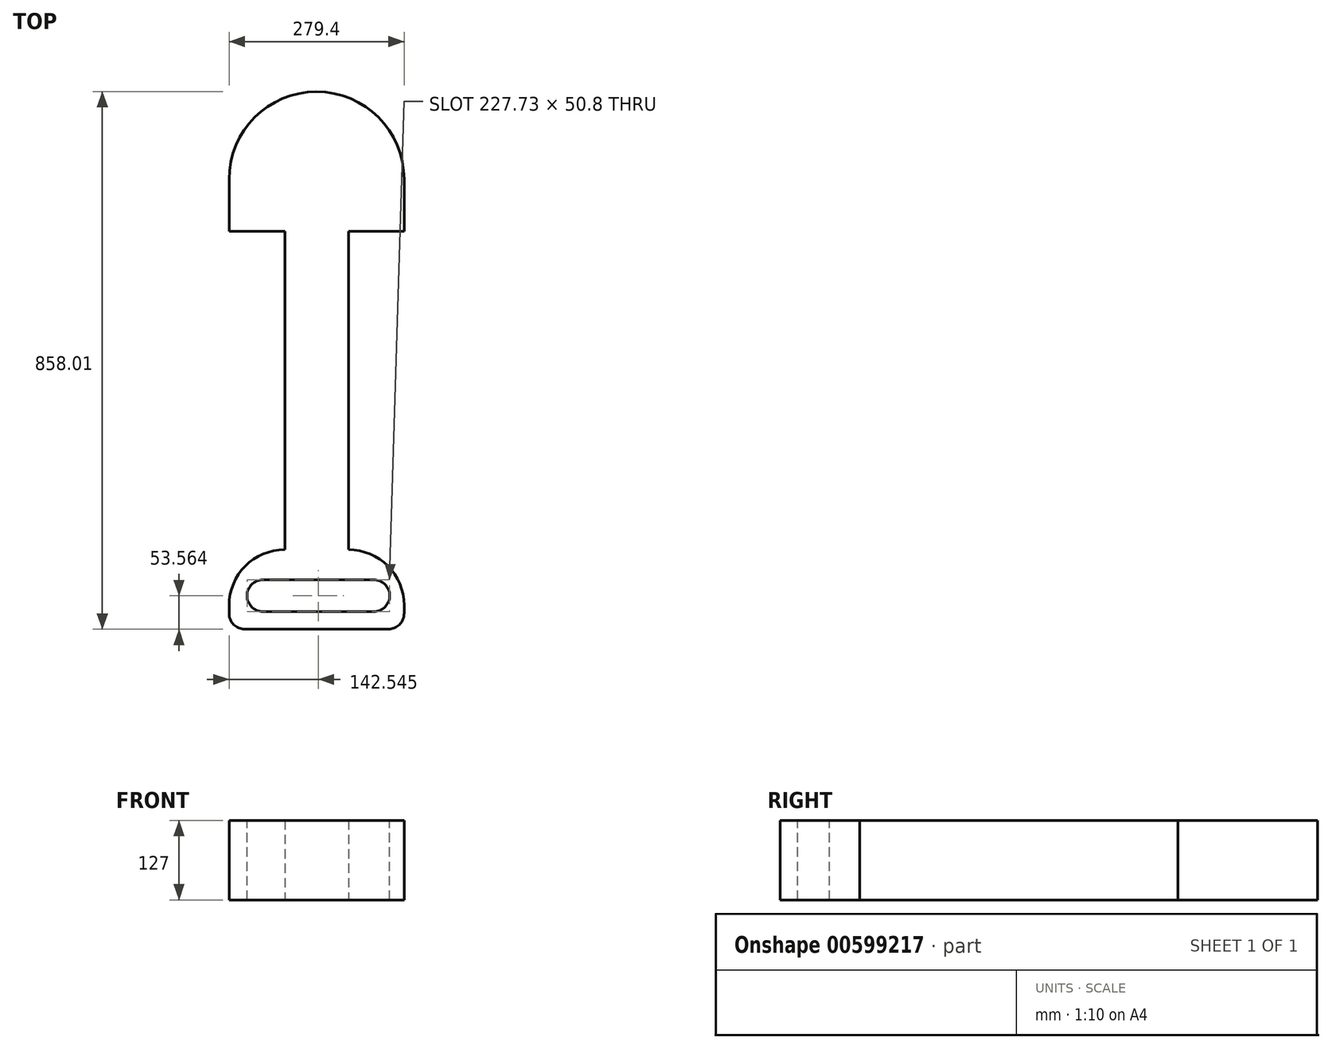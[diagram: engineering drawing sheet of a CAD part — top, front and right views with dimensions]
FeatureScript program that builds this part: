
annotation { "Feature Type Name" : "Feature", "Feature Type Description" : "" }
export const myFeature = defineFeature(function(context is Context, id is Id, definition is map)
    precondition{}
    {
        {
            var Q0;
            Q0=qCreatedBy(makeId("Top.planeOp"),FACE);
            var sketch = newSketch(context, id + "F0", { "sketchPlane" : qUnion([Q0])});
            skLineSegment(sketch, "E0", {"start": v(-139.7, 83.31) * mm, "end": v(-139.7, 0) * mm});
            skLineSegment(sketch, "E1.MirrorCS", {"start": v(139.7, 83.31) * mm, "end": v(139.7, 0) * mm});
            skLineSegment(sketch, "E2", {"start": v(-139.7, 0) * mm, "end": v(139.7, 0) * mm});
            skLineSegment(sketch, "E3", {"start": v(-50.8, 0) * mm, "end": v(-50.8, -508) * mm});
            skLineSegment(sketch, "E4.MirrorCS", {"start": v(50.8, 0) * mm, "end": v(50.8, -508) * mm});
            skLineSegment(sketch, "E5", {"start": v(-50.8, -508) * mm, "end": v(50.8, -508) * mm});
            skLineSegment(sketch, "E6", {"start": v(-50.8, -508) * mm, "end": v(-139.7, -508) * mm});
            skLineSegment(sketch, "E7.MirrorCS", {"start": v(50.8, -508) * mm, "end": v(139.7, -508) * mm});
            skLineSegment(sketch, "E8", {"start": v(-139.7, -508) * mm, "end": v(-139.7, -635) * mm});
            skLineSegment(sketch, "E9.MirrorCS", {"start": v(139.7, -508) * mm, "end": v(139.7, -635) * mm});
            skLineSegment(sketch, "E10", {"start": v(-139.7, -635) * mm, "end": v(139.7, -635) * mm});
            skArc(sketch, "E11", {"start": v(139.7, 83.31) * mm, "mid": v(0, 223.01) * mm, "end": v(-139.7, 83.31) * mm});
            skPoint(sketch, "E12.orphan", {"position": v(-139.7, 363.03) * mm});
            skPoint(sketch, "E13.orphan", {"position": v(139.7, 363.03) * mm});
            skSolve(sketch);
        }
        {
            var Q0;
            Q0 = qSketchRegion(id + "F0", true);
            extrude(context, id + "F1", {"entities" : qUnion([Q0]), "depth" : 127 * mm, "offsetDistance" : 25.4 * mm});
        }
        {
            var Q0;
            Q0=makeQuery(id+"F1.opExtrude","SWEPT_EDGE",EDGE,{"disambiguationData":[OSD([sQuery(id+"F0.wireOp",EDGE,"E7.MirrorCS"),sQuery(id+"F0.wireOp",EDGE,"E9.MirrorCS")])]});
            fillet(context, id + "F2", {"entities" : qUnion([Q0]), "radius" : 88.9 * mm, "tangentPropagation" : true, "allowEdgeOverflow" : false});
        }
        {
            var Q0;
            Q0=makeQuery(id+"F1.opExtrude","SWEPT_EDGE",EDGE,{"disambiguationData":[OSD([sQuery(id+"F0.wireOp",EDGE,"E6"),sQuery(id+"F0.wireOp",EDGE,"E8")])]});
            fillet(context, id + "F3", {"entities" : qUnion([Q0]), "radius" : 88.9 * mm, "tangentPropagation" : true, "allowEdgeOverflow" : false});
        }
        {
            var Q0;
            Q0=makeQuery(id+"F1.opExtrude","CAP_FACE",FACE,{"disambiguationData":[OSD([sQuery(id+"F0.wireOp",EDGE,"E0"),sQuery(id+"F0.wireOp",EDGE,"E1.MirrorCS"),sQuery(id+"F0.wireOp",EDGE,"E2"),sQuery(id+"F0.wireOp",EDGE,"E3"),sQuery(id+"F0.wireOp",EDGE,"E4.MirrorCS"),sQuery(id+"F0.wireOp",EDGE,"E6"),sQuery(id+"F0.wireOp",EDGE,"E7.MirrorCS"),sQuery(id+"F0.wireOp",EDGE,"E8"),sQuery(id+"F0.wireOp",EDGE,"E9.MirrorCS"),sQuery(id+"F0.wireOp",EDGE,"E10"),sQuery(id+"F0.wireOp",EDGE,"E11")])],"isStart":false});
            var sketch = newSketch(context, id + "F4", { "sketchPlane" : qUnion([Q0])});
            skArc(sketch, "E14", {"start": v(-85.62, -556.04) * mm, "mid": v(-111.02, -581.44) * mm, "end": v(-85.62, -606.84) * mm});
            skArc(sketch, "E15", {"start": v(91.31, -606.84) * mm, "mid": v(116.71, -581.44) * mm, "end": v(91.31, -556.04) * mm});
            skLineSegment(sketch, "E16", {"start": v(-85.62, -556.04) * mm, "end": v(91.31, -556.04) * mm});
            skLineSegment(sketch, "E17", {"start": v(-85.62, -606.84) * mm, "end": v(91.31, -606.84) * mm});
            skSolve(sketch);
        }
        {
            var Q0;
            Q0 = qSketchRegion(id + "F4", true);
            extrude(context, id + "F5", {"entities" : qUnion([Q0]), "operationType" : NewBodyOperationType.REMOVE, "endBound" : BoundingType.THROUGH_ALL, "oppositeDirection" : true, "depth" : 25.4 * mm, "offsetDistance" : 25.4 * mm});
        }
        {
            var Q0;
            Q0=makeQuery(id+"F1.opExtrude","SWEPT_EDGE",EDGE,{"disambiguationData":[OSD([sQuery(id+"F0.wireOp",EDGE,"E9.MirrorCS"),sQuery(id+"F0.wireOp",EDGE,"E10")])]});
            fillet(context, id + "F6", {"entities" : qUnion([Q0]), "radius" : 25.4 * mm, "tangentPropagation" : true, "allowEdgeOverflow" : false});
        }
        {
            var Q0;
            Q0=makeQuery(id+"F1.opExtrude","SWEPT_EDGE",EDGE,{"disambiguationData":[OSD([sQuery(id+"F0.wireOp",EDGE,"E8"),sQuery(id+"F0.wireOp",EDGE,"E10")])]});
            fillet(context, id + "F7", {"entities" : qUnion([Q0]), "radius" : 25.4 * mm, "tangentPropagation" : true, "allowEdgeOverflow" : false});
        }
    });
